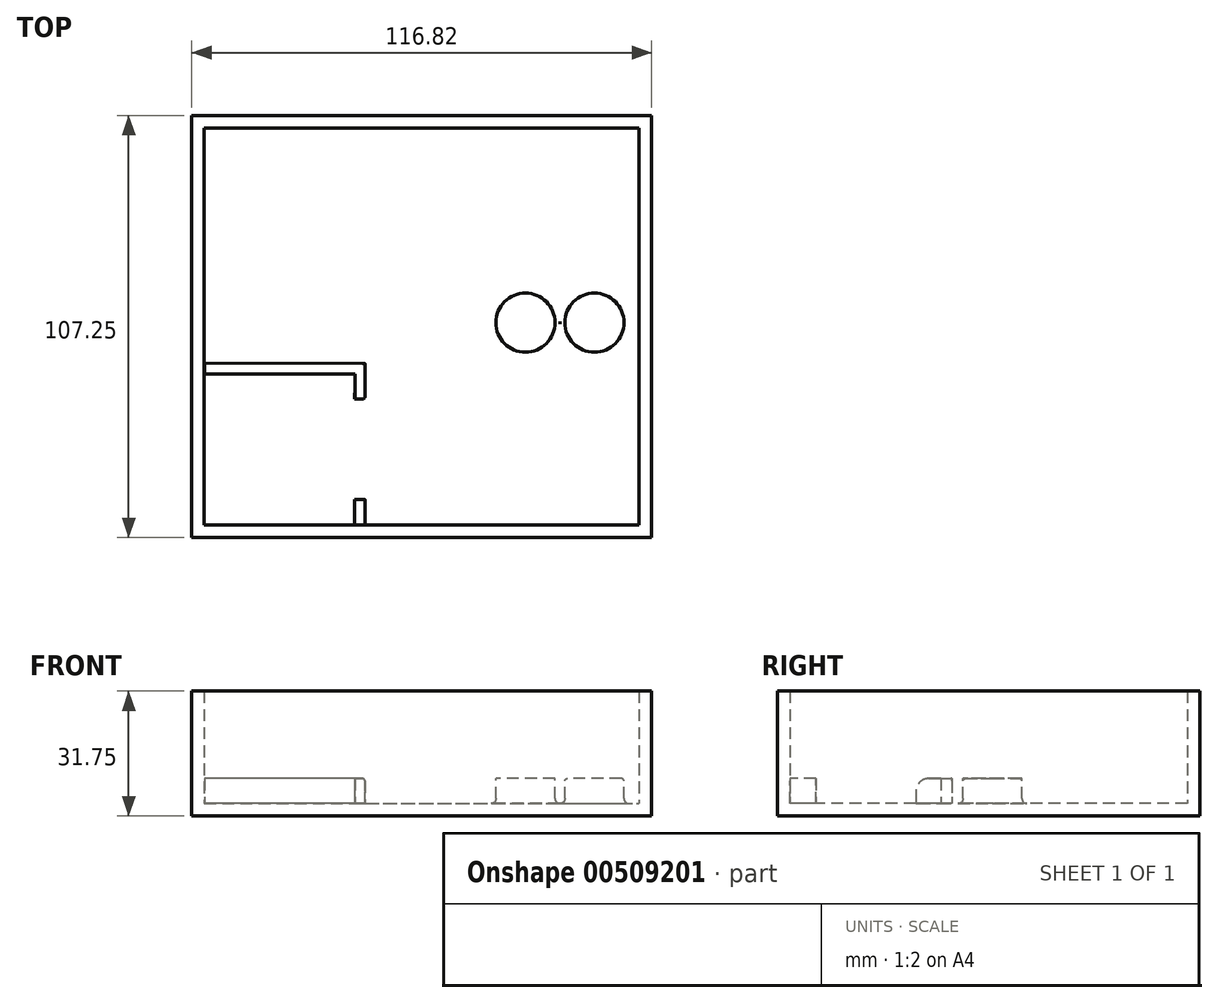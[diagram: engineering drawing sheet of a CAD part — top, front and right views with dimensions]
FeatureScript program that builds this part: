
annotation { "Feature Type Name" : "Feature", "Feature Type Description" : "" }
export const myFeature = defineFeature(function(context is Context, id is Id, definition is map)
    precondition{}
    {
        {
            var Q0;
            Q0=qCreatedBy(makeId("Top.planeOp"),FACE);
            var sketch = newSketch(context, id + "F0", { "sketchPlane" : qUnion([Q0])});
            skLineSegment(sketch, "E0.bottom", {"start": v(-23, -6.49) * mm, "end": v(93.82, -6.49) * mm});
            skLineSegment(sketch, "E0.top", {"start": v(-23, -113.74) * mm, "end": v(93.82, -113.74) * mm});
            skLineSegment(sketch, "E0.left", {"start": v(-23, -6.49) * mm, "end": v(-23, -113.74) * mm});
            skLineSegment(sketch, "E0.right", {"start": v(93.82, -6.49) * mm, "end": v(93.82, -113.74) * mm});
            skSolve(sketch);
        }
        {
            var Q0;
            Q0 = qSketchRegion(id + "F0", true);
            extrude(context, id + "F1", {"entities" : qUnion([Q0]), "depth" : 44.45 * mm});
        }
        {
            var Q0;
            Q0=makeQuery(id+"F1.opExtrude","CAP_FACE",FACE,{"disambiguationData":[OSD([sQuery(id+"F0.wireOp",EDGE,"E0.bottom"),sQuery(id+"F0.wireOp",EDGE,"E0.top"),sQuery(id+"F0.wireOp",EDGE,"E0.left"),sQuery(id+"F0.wireOp",EDGE,"E0.right")])],"isStart":false});
            shell(context, id + "F2", {"entities" : qUnion([Q0]), "thickness" : 3.17 * mm});
        }
        {
            var Q0;
            Q0=makeQuery(id+"F1.opExtrude","CAP_FACE",FACE,{"disambiguationData":[OSD([sQuery(id+"F0.wireOp",EDGE,"E0.bottom"),sQuery(id+"F0.wireOp",EDGE,"E0.top"),sQuery(id+"F0.wireOp",EDGE,"E0.left"),sQuery(id+"F0.wireOp",EDGE,"E0.right")])],"isStart":false});
            extrude(context, id + "F3", {"entities" : qUnion([Q0]), "operationType" : NewBodyOperationType.REMOVE, "oppositeDirection" : true, "depth" : 12.7 * mm});
        }
        {
            var Q0;
            Q0=makeQuery(id+"F2.opShell","OFFSET_FACE",FACE,{"disambiguationData":[OSD([sQuery(id+"F0.wireOp",EDGE,"E0.bottom"),sQuery(id+"F0.wireOp",EDGE,"E0.top"),sQuery(id+"F0.wireOp",EDGE,"E0.left"),sQuery(id+"F0.wireOp",EDGE,"E0.right")])]});
            var sketch = newSketch(context, id + "F4", { "sketchPlane" : qUnion([Q0])});
            skLineSegment(sketch, "E1.bottom", {"start": v(-19.82, -110.56) * mm, "end": v(18.47, -110.56) * mm});
            skLineSegment(sketch, "E1.top", {"start": v(-19.82, -72.19) * mm, "end": v(18.47, -72.19) * mm});
            skLineSegment(sketch, "E1.left", {"start": v(-19.82, -110.56) * mm, "end": v(-19.82, -72.19) * mm});
            skLineSegment(sketch, "E1.right", {"start": v(18.47, -110.56) * mm, "end": v(18.47, -72.19) * mm});
            skSolve(sketch);
        }
        {
            var Q0;
            {var subQ7=sQuery(id+"F4.wireOp",EDGE,"E1.top");Q0=makeQuery(id+"F4.imprint","IMPRINT",FACE,{"disambiguationData":[TD([[makeQuery(id+"F4.imprint","IMPRINT",EDGE,{"derivedFrom":subQ7}),1.0]])]});}
            var sketch = newSketch(context, id + "F5", { "sketchPlane" : qUnion([Q0])});
            skLineSegment(sketch, "E2", {"start": v(18.44, -72.24) * mm, "end": v(21, -72.24) * mm});
            skLineSegment(sketch, "E3", {"start": v(21, -72.24) * mm, "end": v(21, -69.73) * mm});
            skLineSegment(sketch, "E4", {"start": v(-19.79, -72.22) * mm, "end": v(-19.79, -69.66) * mm});
            skLineSegment(sketch, "E5", {"start": v(21, -69.73) * mm, "end": v(-19.79, -69.66) * mm});
            skLineSegment(sketch, "E6", {"start": v(18.34, -110.68) * mm, "end": v(21, -110.69) * mm});
            skLineSegment(sketch, "E7", {"start": v(21, -110.69) * mm, "end": v(21, -72.24) * mm});
            skLineSegment(sketch, "E8", {"start": v(18.44, -72.24) * mm, "end": v(18.34, -110.68) * mm});
            skLineSegment(sketch, "E9", {"start": v(18.44, -72.24) * mm, "end": v(-19.79, -72.22) * mm});
            skSolve(sketch);
        }
        {
            var Q0;
            Q0 = qSketchRegion(id + "F5", true);
            extrude(context, id + "F6", {"entities" : qUnion([Q0]), "operationType" : NewBodyOperationType.ADD, "depth" : 6.35 * mm});
        }
        {
            var Q0;
            Q0=makeQuery(id+"F6.opExtrude","CAP_FACE",FACE,{"disambiguationData":[OSD([sQuery(id+"F5.wireOp",EDGE,"E3"),sQuery(id+"F5.wireOp",EDGE,"E4"),sQuery(id+"F5.wireOp",EDGE,"E5"),sQuery(id+"F5.wireOp",EDGE,"E6"),sQuery(id+"F5.wireOp",EDGE,"E7"),sQuery(id+"F5.wireOp",EDGE,"E8"),sQuery(id+"F5.wireOp",EDGE,"E9")])],"isStart":false});
            var sketch = newSketch(context, id + "F7", { "sketchPlane" : qUnion([Q0])});
            skLineSegment(sketch, "E10", {"start": v(18.34, -110.56) * mm, "end": v(18.35, -104.01) * mm});
            skLineSegment(sketch, "E11", {"start": v(18.44, -72.24) * mm, "end": v(18.42, -78.57) * mm});
            skLineSegment(sketch, "E12.bottom", {"start": v(18.35, -104.01) * mm, "end": v(21, -104.01) * mm});
            skLineSegment(sketch, "E12.top", {"start": v(18.35, -78.57) * mm, "end": v(21, -78.57) * mm});
            skLineSegment(sketch, "E12.left", {"start": v(18.35, -104.01) * mm, "end": v(18.35, -78.57) * mm});
            skLineSegment(sketch, "E12.right", {"start": v(21, -104.01) * mm, "end": v(21, -78.57) * mm});
            skSolve(sketch);
        }
        {
            var Q0;
            {var subQ3=sQuery(id+"F7.wireOp",EDGE,"E12.left");Q0=makeQuery(id+"F7.imprint","IMPRINT",FACE,{"disambiguationData":[TD([[makeQuery(id+"F7.imprint","IMPRINT",EDGE,{"derivedFrom":subQ3}),-1.0]])]});}
            var Q1;
            {var subQ0=sQuery(id+"F7.wireOp",EDGE,"E12.bottom");Q1=makeQuery(id+"F7.imprint","IMPRINT",FACE,{"disambiguationData":[TD([[makeQuery(id+"F7.imprint","IMPRINT",EDGE,{"derivedFrom":subQ0}),1.0]])]});}
            extrude(context, id + "F8", {"entities" : qUnion([Q0, Q1]), "operationType" : NewBodyOperationType.REMOVE, "oppositeDirection" : true, "depth" : 6.35 * mm});
        }
        {
            var Q0;
            Q0=makeQuery(id+"F8.boolean.opBoolean","COPY",EDGE,{"derivedFrom":makeQuery(id+"F8.opExtrude","CAP_EDGE",EDGE,{"disambiguationData":[OSD([sQuery(id+"F7.wireOp",EDGE,"E12.bottom")])],"isStart":true})});
            var Q1;
            Q1=makeQuery(id+"F8.boolean.opBoolean","COPY",EDGE,{"derivedFrom":makeQuery(id+"F8.opExtrude","CAP_EDGE",EDGE,{"disambiguationData":[OSD([sQuery(id+"F7.wireOp",EDGE,"E12.top")])],"isStart":true})});
            fillet(context, id + "F9", {"entities" : qUnion([Q0, Q1]), "radius" : 3.17 * mm, "tangentPropagation" : true, "allowEdgeOverflow" : false});
        }
        {
            var Q0;
            {var subQ7=sQuery(id+"F4.wireOp",EDGE,"E1.top");Q0=makeQuery(id+"F4.imprint","IMPRINT",FACE,{"disambiguationData":[TD([[makeQuery(id+"F4.imprint","IMPRINT",EDGE,{"derivedFrom":subQ7}),1.0]])]});}
            var sketch = newSketch(context, id + "F10", { "sketchPlane" : qUnion([Q0])});
            skLineSegment(sketch, "E13", {"start": v(-19.76, -9.7) * mm, "end": v(-19.76, -48.6) * mm});
            skLineSegment(sketch, "E14", {"start": v(-19.76, -48.6) * mm, "end": v(90.67, -48.6) * mm});
            skLineSegment(sketch, "E15.bottom", {"start": v(90.67, -48.6) * mm, "end": v(-19.8, -48.6) * mm});
            skLineSegment(sketch, "E15.top", {"start": v(90.67, -69.65) * mm, "end": v(-19.8, -69.65) * mm});
            skLineSegment(sketch, "E15.left", {"start": v(90.67, -48.6) * mm, "end": v(90.67, -69.65) * mm});
            skLineSegment(sketch, "E15.right", {"start": v(-19.8, -48.6) * mm, "end": v(-19.8, -69.65) * mm});
            skSolve(sketch);
        }
        {
            var Q0;
            Q0 = qSketchRegion(id + "F10", true);
            extrude(context, id + "F11", {"entities" : qUnion([Q0]), "operationType" : NewBodyOperationType.ADD, "depth" : 6.35 * mm});
        }
        {
            var Q0;
            Q0=makeQuery(id+"F11.opExtrude","CAP_FACE",FACE,{"disambiguationData":[OSD([sQuery(id+"F10.wireOp",EDGE,"E15.bottom"),sQuery(id+"F10.wireOp",EDGE,"E15.top"),sQuery(id+"F10.wireOp",EDGE,"E15.left"),sQuery(id+"F10.wireOp",EDGE,"E15.right")])],"isStart":false});
            var sketch = newSketch(context, id + "F12", { "sketchPlane" : qUnion([Q0])});
            skLineSegment(sketch, "E16", {"start": v(-19.82, -59.13) * mm, "end": v(90.65, -59.13) * mm});
            skCircle(sketch, "E17", {"center": v(-8.33, -59.13) * mm, "radius": 7.5 * mm});
            skCircle(sketch, "E18.1.0.0", {"center": v(9.2, -59.13) * mm, "radius": 7.5 * mm});
            skCircle(sketch, "E18.2.0.0", {"center": v(26.72, -59.13) * mm, "radius": 7.5 * mm});
            skCircle(sketch, "E18.3.0.0", {"center": v(44.25, -59.13) * mm, "radius": 7.5 * mm});
            skCircle(sketch, "E18.4.0.0", {"center": v(61.77, -59.13) * mm, "radius": 7.5 * mm});
            skCircle(sketch, "E18.5.0.0", {"center": v(79.3, -59.13) * mm, "radius": 7.5 * mm});
            skLineSegment(sketch, "E18.direction1", {"start": v(-8.33, -59.13) * mm, "end": v(9.2, -59.13) * mm, "construction": true});
            skSolve(sketch);
        }
        {
            var Q0;
            {var subQ0=sQuery(id+"F12.wireOp",EDGE,"E18.5.0.0");var subQ1=sQuery(id+"F12.wireOp",EDGE,"E16");var subQ2=makeQuery(id+"F12.imprint","INTERSECT",VERTEX,{"disambiguationData":[OD(0.0)],"derivedFrom":[subQ1,subQ0]});Q0=makeQuery(id+"F12.imprint","IMPRINT",FACE,{"disambiguationData":[TD([[makeQuery(id+"F12.imprint","IMPRINT",EDGE,{"disambiguationData":[TD([[subQ2,-1.0]])],"derivedFrom":subQ1}),1.0]])]});}
            var Q1;
            {var subQ0=sQuery(id+"F12.wireOp",EDGE,"E18.5.0.0");var subQ1=sQuery(id+"F12.wireOp",EDGE,"E16");var subQ2=makeQuery(id+"F12.imprint","INTERSECT",VERTEX,{"disambiguationData":[OD(0.0)],"derivedFrom":[subQ1,subQ0]});Q1=makeQuery(id+"F12.imprint","IMPRINT",FACE,{"disambiguationData":[TD([[makeQuery(id+"F12.imprint","IMPRINT",EDGE,{"disambiguationData":[TD([[subQ2,-1.0]])],"derivedFrom":subQ1}),-1.0]])]});}
            var Q2;
            {var subQ0=sQuery(id+"F12.wireOp",EDGE,"E18.4.0.0");var subQ1=sQuery(id+"F12.wireOp",EDGE,"E16");var subQ2=makeQuery(id+"F12.imprint","INTERSECT",VERTEX,{"disambiguationData":[OD(0.0)],"derivedFrom":[subQ1,subQ0]});Q2=makeQuery(id+"F12.imprint","IMPRINT",FACE,{"disambiguationData":[TD([[makeQuery(id+"F12.imprint","IMPRINT",EDGE,{"disambiguationData":[TD([[subQ2,-1.0]])],"derivedFrom":subQ1}),-1.0]])]});}
            var Q3;
            {var subQ0=sQuery(id+"F12.wireOp",EDGE,"E18.4.0.0");var subQ1=sQuery(id+"F12.wireOp",EDGE,"E16");var subQ2=makeQuery(id+"F12.imprint","INTERSECT",VERTEX,{"disambiguationData":[OD(0.0)],"derivedFrom":[subQ1,subQ0]});Q3=makeQuery(id+"F12.imprint","IMPRINT",FACE,{"disambiguationData":[TD([[makeQuery(id+"F12.imprint","IMPRINT",EDGE,{"disambiguationData":[TD([[subQ2,-1.0]])],"derivedFrom":subQ1}),1.0]])]});}
            var Q4;
            {var subQ0=sQuery(id+"F12.wireOp",EDGE,"E18.3.0.0");var subQ1=sQuery(id+"F12.wireOp",EDGE,"E16");var subQ2=makeQuery(id+"F12.imprint","INTERSECT",VERTEX,{"disambiguationData":[OD(0.0)],"derivedFrom":[subQ1,subQ0]});Q4=makeQuery(id+"F12.imprint","IMPRINT",FACE,{"disambiguationData":[TD([[makeQuery(id+"F12.imprint","IMPRINT",EDGE,{"disambiguationData":[TD([[subQ2,-1.0]])],"derivedFrom":subQ1}),-1.0]])]});}
            var Q5;
            {var subQ0=sQuery(id+"F12.wireOp",EDGE,"E18.3.0.0");var subQ1=sQuery(id+"F12.wireOp",EDGE,"E16");var subQ2=makeQuery(id+"F12.imprint","INTERSECT",VERTEX,{"disambiguationData":[OD(0.0)],"derivedFrom":[subQ1,subQ0]});Q5=makeQuery(id+"F12.imprint","IMPRINT",FACE,{"disambiguationData":[TD([[makeQuery(id+"F12.imprint","IMPRINT",EDGE,{"disambiguationData":[TD([[subQ2,-1.0]])],"derivedFrom":subQ1}),1.0]])]});}
            var Q6;
            {var subQ0=sQuery(id+"F12.wireOp",EDGE,"E18.2.0.0");var subQ1=sQuery(id+"F12.wireOp",EDGE,"E16");var subQ2=makeQuery(id+"F12.imprint","INTERSECT",VERTEX,{"disambiguationData":[OD(0.0)],"derivedFrom":[subQ1,subQ0]});Q6=makeQuery(id+"F12.imprint","IMPRINT",FACE,{"disambiguationData":[TD([[makeQuery(id+"F12.imprint","IMPRINT",EDGE,{"disambiguationData":[TD([[subQ2,-1.0]])],"derivedFrom":subQ1}),-1.0]])]});}
            var Q7;
            {var subQ0=sQuery(id+"F12.wireOp",EDGE,"E18.2.0.0");var subQ1=sQuery(id+"F12.wireOp",EDGE,"E16");var subQ2=makeQuery(id+"F12.imprint","INTERSECT",VERTEX,{"disambiguationData":[OD(0.0)],"derivedFrom":[subQ1,subQ0]});Q7=makeQuery(id+"F12.imprint","IMPRINT",FACE,{"disambiguationData":[TD([[makeQuery(id+"F12.imprint","IMPRINT",EDGE,{"disambiguationData":[TD([[subQ2,-1.0]])],"derivedFrom":subQ1}),1.0]])]});}
            var Q8;
            {var subQ0=sQuery(id+"F12.wireOp",EDGE,"E18.1.0.0");var subQ1=sQuery(id+"F12.wireOp",EDGE,"E16");var subQ2=makeQuery(id+"F12.imprint","INTERSECT",VERTEX,{"disambiguationData":[OD(0.0)],"derivedFrom":[subQ1,subQ0]});Q8=makeQuery(id+"F12.imprint","IMPRINT",FACE,{"disambiguationData":[TD([[makeQuery(id+"F12.imprint","IMPRINT",EDGE,{"disambiguationData":[TD([[subQ2,-1.0]])],"derivedFrom":subQ1}),-1.0]])]});}
            var Q9;
            {var subQ0=sQuery(id+"F12.wireOp",EDGE,"E18.1.0.0");var subQ1=sQuery(id+"F12.wireOp",EDGE,"E16");var subQ2=makeQuery(id+"F12.imprint","INTERSECT",VERTEX,{"disambiguationData":[OD(0.0)],"derivedFrom":[subQ1,subQ0]});Q9=makeQuery(id+"F12.imprint","IMPRINT",FACE,{"disambiguationData":[TD([[makeQuery(id+"F12.imprint","IMPRINT",EDGE,{"disambiguationData":[TD([[subQ2,-1.0]])],"derivedFrom":subQ1}),1.0]])]});}
            var Q10;
            {var subQ0=sQuery(id+"F12.wireOp",EDGE,"E17");var subQ1=sQuery(id+"F12.wireOp",EDGE,"E16");var subQ2=makeQuery(id+"F12.imprint","INTERSECT",VERTEX,{"disambiguationData":[OD(0.0)],"derivedFrom":[subQ1,subQ0]});Q10=makeQuery(id+"F12.imprint","IMPRINT",FACE,{"disambiguationData":[TD([[makeQuery(id+"F12.imprint","IMPRINT",EDGE,{"disambiguationData":[TD([[subQ2,-1.0]])],"derivedFrom":subQ1}),-1.0]])]});}
            var Q11;
            {var subQ0=sQuery(id+"F12.wireOp",EDGE,"E17");var subQ1=sQuery(id+"F12.wireOp",EDGE,"E16");var subQ2=makeQuery(id+"F12.imprint","INTERSECT",VERTEX,{"disambiguationData":[OD(0.0)],"derivedFrom":[subQ1,subQ0]});Q11=makeQuery(id+"F12.imprint","IMPRINT",FACE,{"disambiguationData":[TD([[makeQuery(id+"F12.imprint","IMPRINT",EDGE,{"disambiguationData":[TD([[subQ2,-1.0]])],"derivedFrom":subQ1}),1.0]])]});}
            extrude(context, id + "F13", {"entities" : qUnion([Q0, Q1, Q2, Q3, Q4, Q5, Q6, Q7, Q8, Q9, Q10, Q11]), "operationType" : NewBodyOperationType.REMOVE, "oppositeDirection" : true, "depth" : 6.35 * mm});
        }
        {
            var Q0;
            Q0=makeQuery(id+"F13.boolean.opBoolean","COPY",EDGE,{"derivedFrom":makeQuery(id+"F13.opExtrude","CAP_EDGE",EDGE,{"disambiguationData":[OSD([sQuery(id+"F12.wireOp",EDGE,"E18.5.0.0")])],"isStart":true})});
            var Q1;
            Q1=makeQuery(id+"F13.boolean.opBoolean","COPY",EDGE,{"derivedFrom":makeQuery(id+"F13.opExtrude","CAP_EDGE",EDGE,{"disambiguationData":[OSD([sQuery(id+"F12.wireOp",EDGE,"E18.4.0.0")])],"isStart":true})});
            var Q2;
            Q2=makeQuery(id+"F13.boolean.opBoolean","COPY",EDGE,{"derivedFrom":makeQuery(id+"F13.opExtrude","CAP_EDGE",EDGE,{"disambiguationData":[OSD([sQuery(id+"F12.wireOp",EDGE,"E18.3.0.0")])],"isStart":true})});
            var Q3;
            Q3=makeQuery(id+"F13.boolean.opBoolean","COPY",EDGE,{"derivedFrom":makeQuery(id+"F13.opExtrude","CAP_EDGE",EDGE,{"disambiguationData":[OSD([sQuery(id+"F12.wireOp",EDGE,"E18.2.0.0")])],"isStart":true})});
            var Q4;
            Q4=makeQuery(id+"F13.boolean.opBoolean","COPY",EDGE,{"derivedFrom":makeQuery(id+"F13.opExtrude","CAP_EDGE",EDGE,{"disambiguationData":[OSD([sQuery(id+"F12.wireOp",EDGE,"E18.1.0.0")])],"isStart":true})});
            var Q5;
            Q5=makeQuery(id+"F13.boolean.opBoolean","COPY",EDGE,{"derivedFrom":makeQuery(id+"F13.opExtrude","CAP_EDGE",EDGE,{"disambiguationData":[OSD([sQuery(id+"F12.wireOp",EDGE,"E17")])],"isStart":true})});
            fillet(context, id + "F14", {"entities" : qUnion([Q0, Q1, Q2, Q3, Q4, Q5]), "radius" : 0.64 * mm, "tangentPropagation" : true, "allowEdgeOverflow" : false});
        }
        {
            var Q0;
            Q0=makeQuery(id+"F13.boolean.opBoolean","COPY",EDGE,{"derivedFrom":makeQuery(id+"F13.opExtrude","CAP_EDGE",EDGE,{"disambiguationData":[OSD([sQuery(id+"F12.wireOp",EDGE,"E17")])],"isStart":false})});
            var Q1;
            Q1=makeQuery(id+"F13.boolean.opBoolean","COPY",EDGE,{"derivedFrom":makeQuery(id+"F13.opExtrude","CAP_EDGE",EDGE,{"disambiguationData":[OSD([sQuery(id+"F12.wireOp",EDGE,"E18.1.0.0")])],"isStart":false})});
            var Q2;
            Q2=makeQuery(id+"F13.boolean.opBoolean","COPY",EDGE,{"derivedFrom":makeQuery(id+"F13.opExtrude","CAP_EDGE",EDGE,{"disambiguationData":[OSD([sQuery(id+"F12.wireOp",EDGE,"E18.2.0.0")])],"isStart":false})});
            var Q3;
            Q3=makeQuery(id+"F13.boolean.opBoolean","COPY",EDGE,{"derivedFrom":makeQuery(id+"F13.opExtrude","CAP_EDGE",EDGE,{"disambiguationData":[OSD([sQuery(id+"F12.wireOp",EDGE,"E18.3.0.0")])],"isStart":false})});
            var Q4;
            Q4=makeQuery(id+"F13.boolean.opBoolean","COPY",EDGE,{"derivedFrom":makeQuery(id+"F13.opExtrude","CAP_EDGE",EDGE,{"disambiguationData":[OSD([sQuery(id+"F12.wireOp",EDGE,"E18.5.0.0")])],"isStart":false})});
            var Q5;
            Q5=makeQuery(id+"F13.boolean.opBoolean","COPY",EDGE,{"derivedFrom":makeQuery(id+"F13.opExtrude","CAP_EDGE",EDGE,{"disambiguationData":[OSD([sQuery(id+"F12.wireOp",EDGE,"E18.4.0.0")])],"isStart":false})});
            fillet(context, id + "F15", {"entities" : qUnion([Q0, Q1, Q2, Q3, Q4, Q5]), "radius" : 1.27 * mm, "tangentPropagation" : true, "allowEdgeOverflow" : false});
        }
        {
            var Q0;
            Q0=makeQuery(id+"F6.opExtrude","SWEPT_FACE",FACE,{"disambiguationData":[OSD([sQuery(id+"F5.wireOp",EDGE,"E5")])]});
            extrude(context, id + "F16", {"entities" : qUnion([Q0]), "operationType" : NewBodyOperationType.ADD, "depth" : 0.25 * mm});
        }
        {
            var Q0;
            {var subQ0=sQuery(id+"F10.wireOp",EDGE,"E15.top");Q0=makeQuery(id+"F16.boolean.opBoolean","SPLIT",EDGE,{"disambiguationData":[TD([makeQuery(id+"F2.opShell","OFFSET_FACE",FACE,{"disambiguationData":[OSD([sQuery(id+"F0.wireOp",EDGE,"E0.right")])]})])],"derivedFrom":makeQuery(id+"F11.opExtrude","CAP_EDGE",EDGE,{"disambiguationData":[OSD([subQ0])],"isStart":false})});}
            var Q1;
            {var subQ0=sQuery(id+"F5.wireOp",EDGE,"E7");var subQ1=sQuery(id+"F5.wireOp",EDGE,"E5");var subQ2=sQuery(id+"F5.wireOp",EDGE,"E3");Q1=makeQuery(id+"F8.boolean.opBoolean","SPLIT",EDGE,{"disambiguationData":[TD([makeQuery(id+"F6.opExtrude","SWEPT_FACE",FACE,{"disambiguationData":[OSD([subQ1])]})])],"derivedFrom":makeQuery(id+"F6.opExtrude","CAP_EDGE",EDGE,{"disambiguationData":[OSD([subQ2,subQ0])],"isStart":false})});}
            var Q2;
            {var subQ0=sQuery(id+"F7.wireOp",EDGE,"E12.top");var subQ1=sQuery(id+"F5.wireOp",EDGE,"E7");var subQ2=sQuery(id+"F5.wireOp",EDGE,"E5");var subQ3=sQuery(id+"F5.wireOp",EDGE,"E3");Q2=makeQuery(id+"F9.opFillet","BLEND_EDGE",EDGE,{"blendedFrom":[makeQuery(id+"F8.boolean.opBoolean","COPY",EDGE,{"derivedFrom":makeQuery(id+"F8.opExtrude","CAP_EDGE",EDGE,{"disambiguationData":[OSD([subQ0])],"isStart":true})}),makeQuery(id+"F8.boolean.opBoolean","SPLIT",FACE,{"disambiguationData":[TD([makeQuery(id+"F6.opExtrude","SWEPT_FACE",FACE,{"disambiguationData":[OSD([subQ2])]})])],"derivedFrom":makeQuery(id+"F6.opExtrude","SWEPT_FACE",FACE,{"disambiguationData":[OSD([subQ3,subQ1])]})})],"blendedInto":[makeQuery(id+"F8.boolean.opBoolean","SPLIT",FACE,{"disambiguationData":[TD([makeQuery(id+"F6.opExtrude","SWEPT_FACE",FACE,{"disambiguationData":[OSD([subQ2])]})])],"derivedFrom":makeQuery(id+"F6.opExtrude","SWEPT_FACE",FACE,{"disambiguationData":[OSD([subQ3,subQ1])]})})]});}
            var Q3;
            Q3=makeQuery(id+"F8.boolean.opBoolean","COPY",EDGE,{"derivedFrom":makeQuery(id+"F8.opExtrude","SWEPT_EDGE",EDGE,{"disambiguationData":[OSD([sQuery(id+"F5.wireOp",EDGE,"E3"),sQuery(id+"F5.wireOp",EDGE,"E7"),sQuery(id+"F7.wireOp",EDGE,"E12.top"),sQuery(id+"F7.wireOp",EDGE,"E12.right")])]})});
            var Q4;
            {var subQ0=sQuery(id+"F5.wireOp",EDGE,"E7");var subQ1=sQuery(id+"F5.wireOp",EDGE,"E3");Q4=makeQuery(id+"F8.boolean.opBoolean","SPLIT",EDGE,{"disambiguationData":[TD([makeQuery(id+"F2.opShell","OFFSET_FACE",FACE,{"disambiguationData":[OSD([sQuery(id+"F0.wireOp",EDGE,"E0.top")])]})])],"derivedFrom":makeQuery(id+"F6.opExtrude","CAP_EDGE",EDGE,{"disambiguationData":[OSD([subQ1,subQ0])],"isStart":false})});}
            var Q5;
            Q5=makeQuery(id+"F11.opExtrude","CAP_EDGE",EDGE,{"disambiguationData":[OSD([sQuery(id+"F10.wireOp",EDGE,"E15.bottom")])],"isStart":false});
            fillet(context, id + "F17", {"entities" : qUnion([Q0, Q1, Q2, Q3, Q4, Q5]), "radius" : 0.64 * mm, "tangentPropagation" : true, "allowEdgeOverflow" : false});
        }
    });
